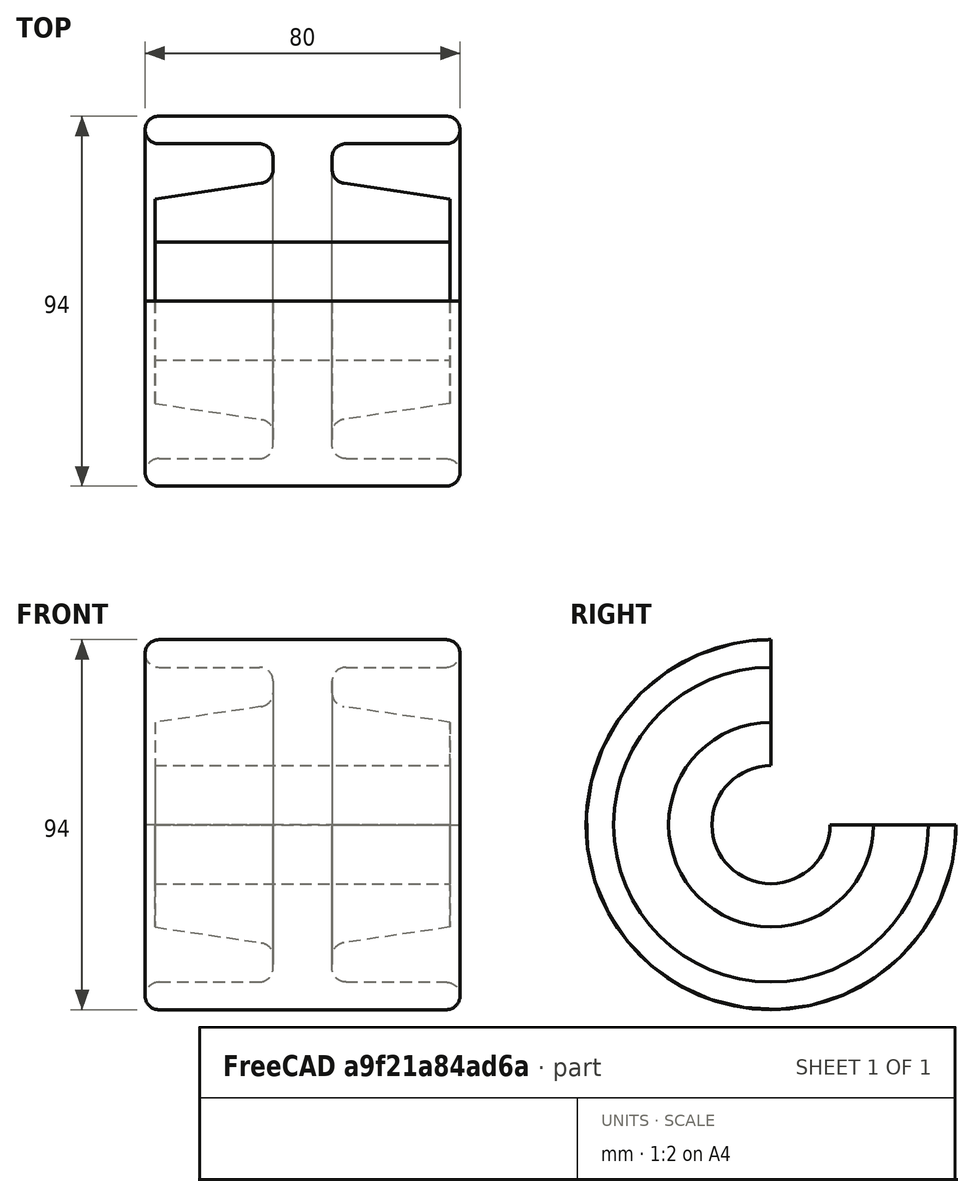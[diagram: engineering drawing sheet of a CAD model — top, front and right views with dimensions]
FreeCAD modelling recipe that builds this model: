
FCSTD DOCUMENT  (FreeCAD 0.16R)
Label: ejer13
License: All rights reserved
LicenseURL: http://en.wikipedia.org/wiki/All_rights_reserved
objects: Sketcher::SketchObject×1, PartDesign::Revolution×1
note: 3 computed .brp shape members not serialized (recipe doc carries the construction recipe); baked Part::Feature solids carry a one-line shape summary decoded from their .brp

FEATURE [Sketcher::SketchObject] Sketch
  Placement = pos=(0,0,0) rot=(-1,0,0;4.71239rad)
  sketch-geometry (16):
    g0: LineSegment StartX=-37.5 StartY=15 StartZ=0 EndX=37.5 EndY=15 EndZ=0
    g1: LineSegment StartX=37.5 StartY=15 StartZ=0 EndX=37.5 EndY=26 EndZ=0
    g2: LineSegment StartX=37.5 StartY=26 StartZ=0 EndX=10.4873 EndY=30 EndZ=0
    g3: LineSegment StartX=7.5 StartY=33.4622 StartZ=0 EndX=7.5 EndY=36.5 EndZ=0
    g4: LineSegment StartX=11 StartY=40 StartZ=0 EndX=36.5 EndY=40 EndZ=0
    g5: LineSegment StartX=36.5 StartY=47 StartZ=0 EndX=-36.5 EndY=47 EndZ=0
    g6: LineSegment StartX=-36.5 StartY=40 StartZ=0 EndX=-11 EndY=40 EndZ=0
    g7: LineSegment StartX=-7.5 StartY=36.5 StartZ=0 EndX=-7.5 EndY=33.4622 EndZ=0
    g8: LineSegment StartX=-10.4873 StartY=30 StartZ=0 EndX=-37.5 EndY=26 EndZ=0
    g9: LineSegment StartX=-37.5 StartY=26 StartZ=0 EndX=-37.5 EndY=15 EndZ=0
    g10: ArcOfCircle CenterX=36.5 CenterY=43.5 CenterZ=0 NormalX=0 NormalY=0 NormalZ=1 Radius=3.5 StartAngle=4.71239 EndAngle=7.85398
    g11: ArcOfCircle CenterX=-36.5 CenterY=43.5 CenterZ=0 NormalX=0 NormalY=0 NormalZ=1 Radius=3.5 StartAngle=1.5708 EndAngle=4.71238
    g12: ArcOfCircle CenterX=11 CenterY=36.5 CenterZ=0 NormalX=0 NormalY=0 NormalZ=1 Radius=3.5 StartAngle=1.5708 EndAngle=3.14159
    g13: ArcOfCircle CenterX=11 CenterY=33.4622 CenterZ=0 NormalX=0 NormalY=0 NormalZ=1 Radius=3.5 StartAngle=3.14159 EndAngle=4.56538
    g14: ArcOfCircle CenterX=-11 CenterY=33.4622 CenterZ=0 NormalX=0 NormalY=0 NormalZ=1 Radius=3.5 StartAngle=4.8594 EndAngle=6.28319
    g15: ArcOfCircle CenterX=-11 CenterY=36.5 CenterZ=0 NormalX=0 NormalY=0 NormalZ=1 Radius=3.5 StartAngle=0 EndAngle=1.5708
  constraints (44):
    c: Horizontal(g0)
    c: Coincident(g0,g1)
    c: Vertical(g1)
    c: Coincident(g1,g2)
    c: Vertical(g3)
    c: Horizontal(g5)
    c: Vertical(g7)
    c: Coincident(g8,g9)
    c: Coincident(g9,g0)
    c: Vertical(g9)
    c: Coincident(g10,g5)
    c: Coincident(g10,g4)
    c: Coincident(g11,g5)
    c: Radius(g11) = 3.5
    c: Radius(g10) = 3.5
    c: Tangent(g3,g12) = 1.5708
    c: Tangent(g4,g12) = 1.5708
    c: Tangent(g2,g13) = 1.5708
    c: Tangent(g3,g13) = 1.5708
    c: Tangent(g8,g14) = 1.5708
    c: Tangent(g7,g14) = 1.5708
    c: Tangent(g6,g15) = 1.5708
    c: Tangent(g7,g15) = 1.5708
    c: Radius(g15) = 3.5
    c: Equal(g15,g14)
    c: Equal(g15,g12)
    c: Equal(g15,g13)
    c: Coincident(g6,g11)
    c: Tangent(g5,g11)
    c: Tangent(g6,g11)
    c: Tangent(g4,g10)
    c: Tangent(g10,g5)
    c: Symmetric(g10,g11,g-2)
    c: DistanceX(g11,g10) = 73
    c: Symmetric(g6,g4,g-2)
    c: Symmetric(g8,g2,g-2)
    c: DistanceY(g0,g4) = 25
    c: Symmetric(g0,g0,g-2)
    c: DistanceX(g0,g0) = 75
    c: DistanceY(g0,g2) = 15
    c: DistanceY(g8,g6) = 10
    c: DistanceY(g-1,g0) = 15
    c: DistanceY(g-1,g1) = 26
    c: DistanceX(g7,g3) = 15
FEATURE [PartDesign::Revolution] Revolution
  Angle = 270
  Axis = (1,0,0)
  Base = (0,0,0)
  Placement = pos=(0,0,0) rot=(-1,0,0;4.71239rad)
  ReferenceAxis = -> Sketch [H_Axis]
  Sketch = -> Sketch
